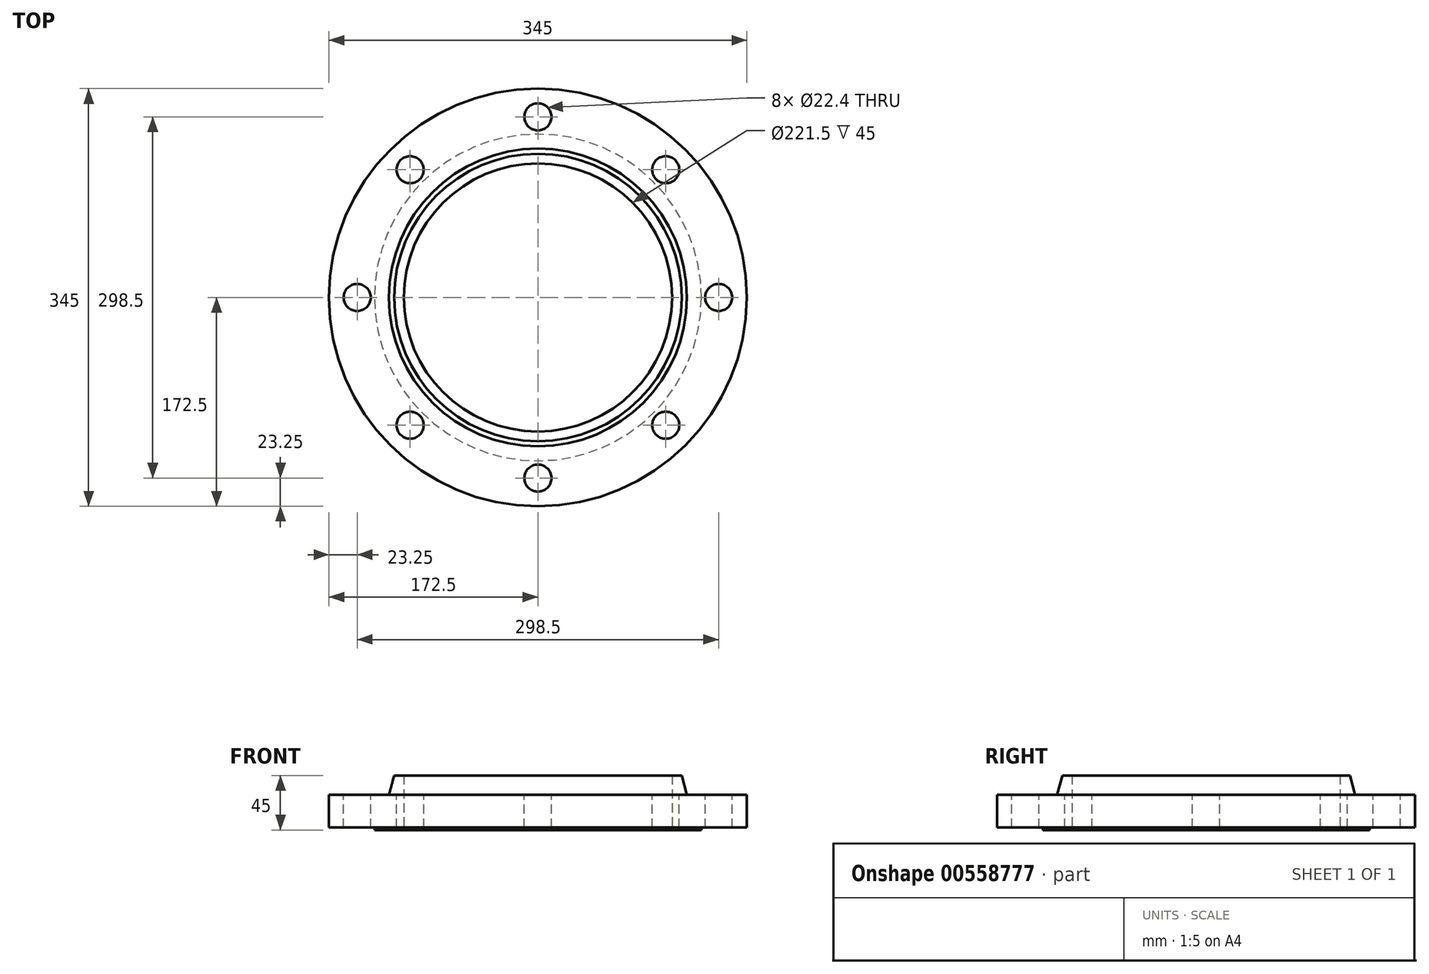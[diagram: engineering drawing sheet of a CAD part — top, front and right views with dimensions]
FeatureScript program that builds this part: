
annotation { "Feature Type Name" : "Feature", "Feature Type Description" : "" }
export const myFeature = defineFeature(function(context is Context, id is Id, definition is map)
    precondition{}
    {
        {
            var Q0;
            Q0=qCreatedBy(makeId("Front.planeOp"),FACE);
            var sketch = newSketch(context, id + "F0", { "sketchPlane" : qUnion([Q0])});
            skLineSegment(sketch, "E0", {"start": v(110.75, 0) * mm, "end": v(134.95, 0) * mm});
            skLineSegment(sketch, "E1", {"start": v(134.95, 0) * mm, "end": v(134.95, 2) * mm});
            skLineSegment(sketch, "E2", {"start": v(134.95, 2) * mm, "end": v(172.5, 2) * mm});
            skLineSegment(sketch, "E3", {"start": v(172.5, 2) * mm, "end": v(172.5, 29) * mm});
            skLineSegment(sketch, "E4", {"start": v(172.5, 29) * mm, "end": v(123, 29) * mm});
            skLineSegment(sketch, "E5", {"start": v(123, 29) * mm, "end": v(118.71, 45) * mm});
            skLineSegment(sketch, "E6", {"start": v(118.71, 45) * mm, "end": v(110.75, 45) * mm});
            skLineSegment(sketch, "E7", {"start": v(110.75, 45) * mm, "end": v(110.75, 0) * mm});
            skLineSegment(sketch, "E8", {"start": v(0, 0) * mm, "end": v(0, 45) * mm});
            skSolve(sketch);
        }
        {
            var Q0;
            Q0=makeQuery(id+"F0.imprint","IMPRINT",FACE,{"disambiguationData":[TD([[makeQuery(id+"F0.imprint","IMPRINT",EDGE,{"derivedFrom":sQuery(id+"F0.wireOp",EDGE,"E0")}),1.0]])]});
            var Q1;
            Q1=sQuery(id+"F0.wireOp",EDGE,"E8");
            revolve(context, id + "F1", {"entities" : qUnion([Q0]), "axis" : qUnion([Q1]), "revolveType" : RevolveType.FULL});
        }
        {
            var Q0;
            Q0=makeQuery(id+"F1.opRevolve","SWEPT_FACE",FACE,{"disambiguationData":[OSD([sQuery(id+"F0.wireOp",EDGE,"E4")])]});
            var sketch = newSketch(context, id + "F2", { "sketchPlane" : qUnion([Q0])});
            skCircle(sketch, "E9", {"center": v(0, 0) * mm, "radius": 149.25 * mm, "construction": true});
            skCircle(sketch, "E10", {"center": v(0, 149.25) * mm, "radius": 11.2 * mm});
            skCircle(sketch, "E11.1.0", {"center": v(-105.54, 105.54) * mm, "radius": 11.2 * mm});
            skCircle(sketch, "E11.2.0", {"center": v(-149.25, 0) * mm, "radius": 11.2 * mm});
            skCircle(sketch, "E11.3.0", {"center": v(-105.54, -105.54) * mm, "radius": 11.2 * mm});
            skCircle(sketch, "E11.4.0", {"center": v(0, -149.25) * mm, "radius": 11.2 * mm});
            skCircle(sketch, "E11.5.0", {"center": v(105.54, -105.54) * mm, "radius": 11.2 * mm});
            skCircle(sketch, "E11.6.0", {"center": v(149.25, 0) * mm, "radius": 11.2 * mm});
            skCircle(sketch, "E11.7.0", {"center": v(105.54, 105.54) * mm, "radius": 11.2 * mm});
            skSolve(sketch);
        }
        {
            var Q0;
            Q0=qSketchRegion(id+"F2",true);
            extrude(context, id + "F3", {"entities" : qUnion([Q0]), "operationType" : NewBodyOperationType.REMOVE, "endBound" : BoundingType.THROUGH_ALL, "oppositeDirection" : true, "depth" : 25 * mm, "offsetDistance" : 25 * mm});
        }
    });
